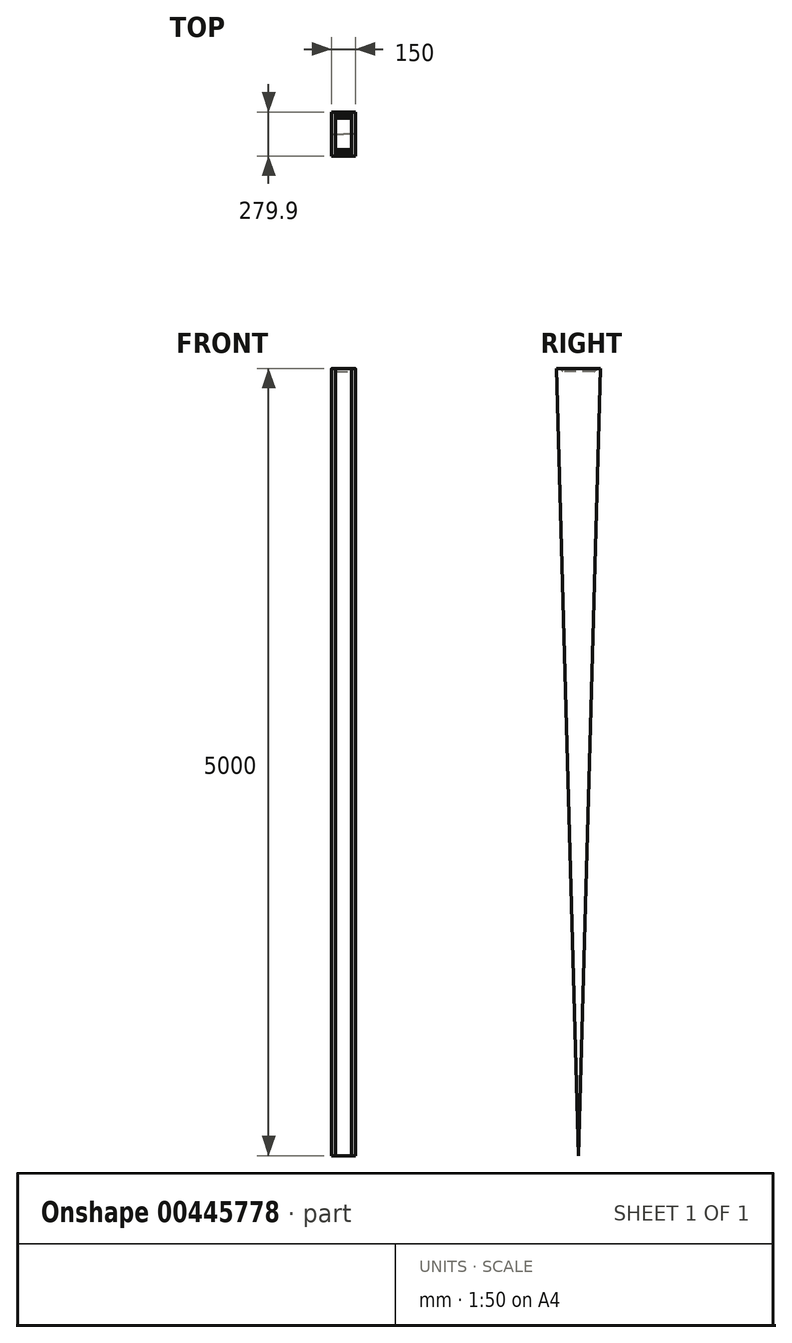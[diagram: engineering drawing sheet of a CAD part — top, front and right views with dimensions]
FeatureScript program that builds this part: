
annotation { "Feature Type Name" : "Feature", "Feature Type Description" : "" }
export const myFeature = defineFeature(function(context is Context, id is Id, definition is map)
    precondition{}
    {
        {
            var Q0;
            Q0=qCreatedBy(makeId("Right.planeOp"),FACE);
            var sketch = newSketch(context, id + "F0", { "sketchPlane" : qUnion([Q0])});
            skArc(sketch, "E0", {"start": v(0, 4980) * mm, "mid": v(-49.8, 4979.75) * mm, "end": v(-99.6, 4979) * mm});
            skLineSegment(sketch, "E1", {"start": v(0, 0) * mm, "end": v(-99.6, 4979) * mm, "construction": true});
            skLineSegment(sketch, "E2", {"start": v(-99.6, 4979) * mm, "end": v(-119.95, 4998.56) * mm});
            skPoint(sketch, "E3.startSnap0", {"position": v(-109.77, 4988.78) * mm});
            skLineSegment(sketch, "E4", {"start": v(0, 0) * mm, "end": v(0, 5000) * mm, "construction": true});
            skLineSegment(sketch, "E5.MirrorCS", {"start": v(99.6, 4979) * mm, "end": v(119.95, 4998.56) * mm});
            skArc(sketch, "E6.MirrorCS", {"start": v(0, 4980) * mm, "mid": v(49.8, 4979.75) * mm, "end": v(99.6, 4979) * mm});
            skArc(sketch, "E7", {"start": v(139.95, 4998.04) * mm, "mid": v(129.95, 4998.31) * mm, "end": v(119.95, 4998.56) * mm});
            skLineSegment(sketch, "E8", {"start": v(-139.95, 4998.04) * mm, "end": v(0, 0) * mm});
            skLineSegment(sketch, "E9.MirrorCS", {"start": v(139.95, 4998.04) * mm, "end": v(0, 0) * mm});
            skArc(sketch, "E10.trimOffspring", {"start": v(-119.95, 4998.56) * mm, "mid": v(-129.95, 4998.31) * mm, "end": v(-139.95, 4998.04) * mm});
            skArc(sketch, "E11", {"start": v(119.95, 4998.56) * mm, "mid": v(0, 5000) * mm, "end": v(-119.95, 4998.56) * mm, "construction": true});
            skSolve(sketch);
        }
        {
            var Q0;
            Q0 = qSketchRegion(id + "F0", true);
            extrude(context, id + "F1", {"entities" : qUnion([Q0]), "endBound" : BoundingType.SYMMETRIC, "depth" : 100 * mm});
        }
        {
            var Q0;
            Q0=makeQuery(id+"F1.opExtrude","CAP_FACE",FACE,{"disambiguationData":[OSD([sQuery(id+"F0.wireOp",EDGE,"E0"),sQuery(id+"F0.wireOp",EDGE,"E2"),sQuery(id+"F0.wireOp",EDGE,"E5.MirrorCS"),sQuery(id+"F0.wireOp",EDGE,"E6.MirrorCS"),sQuery(id+"F0.wireOp",EDGE,"E7"),sQuery(id+"F0.wireOp",EDGE,"E8"),sQuery(id+"F0.wireOp",EDGE,"E9.MirrorCS"),sQuery(id+"F0.wireOp",EDGE,"E10.trimOffspring")])],"isStart":false});
            var sketch = newSketch(context, id + "F2", { "sketchPlane" : qUnion([Q0])});
            skArc(sketch, "E12", {"start": v(139.95, 4998.04) * mm, "mid": v(0, 5000) * mm, "end": v(-139.95, 4998.04) * mm});
            skPoint(sketch, "E12.first.point", {"position": v(-139.95, 4998.04) * mm});
            skPoint(sketch, "E12.second.point", {"position": v(139.95, 4998.04) * mm});
            skPoint(sketch, "E12.third.point", {"position": v(119.95, 4998.56) * mm});
            skLineSegment(sketch, "E13.0", {"start": v(-139.95, 4998.04) * mm, "end": v(0, 0) * mm});
            skLineSegment(sketch, "E14.0", {"start": v(139.95, 4998.04) * mm, "end": v(0, 0) * mm});
            skSolve(sketch);
        }
        {
            var Q0;
            Q0 = qSketchRegion(id + "F2", true);
            extrude(context, id + "F3", {"entities" : qUnion([Q0]), "operationType" : NewBodyOperationType.ADD, "depth" : 25 * mm});
        }
        {
            var Q0;
            Q0=makeQuery(id+"F1.opExtrude","SWEPT_BODY",BODY,{"disambiguationData":[OSD([sQuery(id+"F0.wireOp",EDGE,"E0"),sQuery(id+"F0.wireOp",EDGE,"E2"),sQuery(id+"F0.wireOp",EDGE,"E5.MirrorCS"),sQuery(id+"F0.wireOp",EDGE,"E6.MirrorCS"),sQuery(id+"F0.wireOp",EDGE,"E7"),sQuery(id+"F0.wireOp",EDGE,"E8"),sQuery(id+"F0.wireOp",EDGE,"E9.MirrorCS"),sQuery(id+"F0.wireOp",EDGE,"E10.trimOffspring")])]});
            var Q1;
            Q1=qCreatedBy(makeId("Right.planeOp"),FACE);
            mirror(context, id + "F4", {"entities" : qUnion([Q0]), "mirrorPlane" : qUnion([Q1])});
        }
    });
